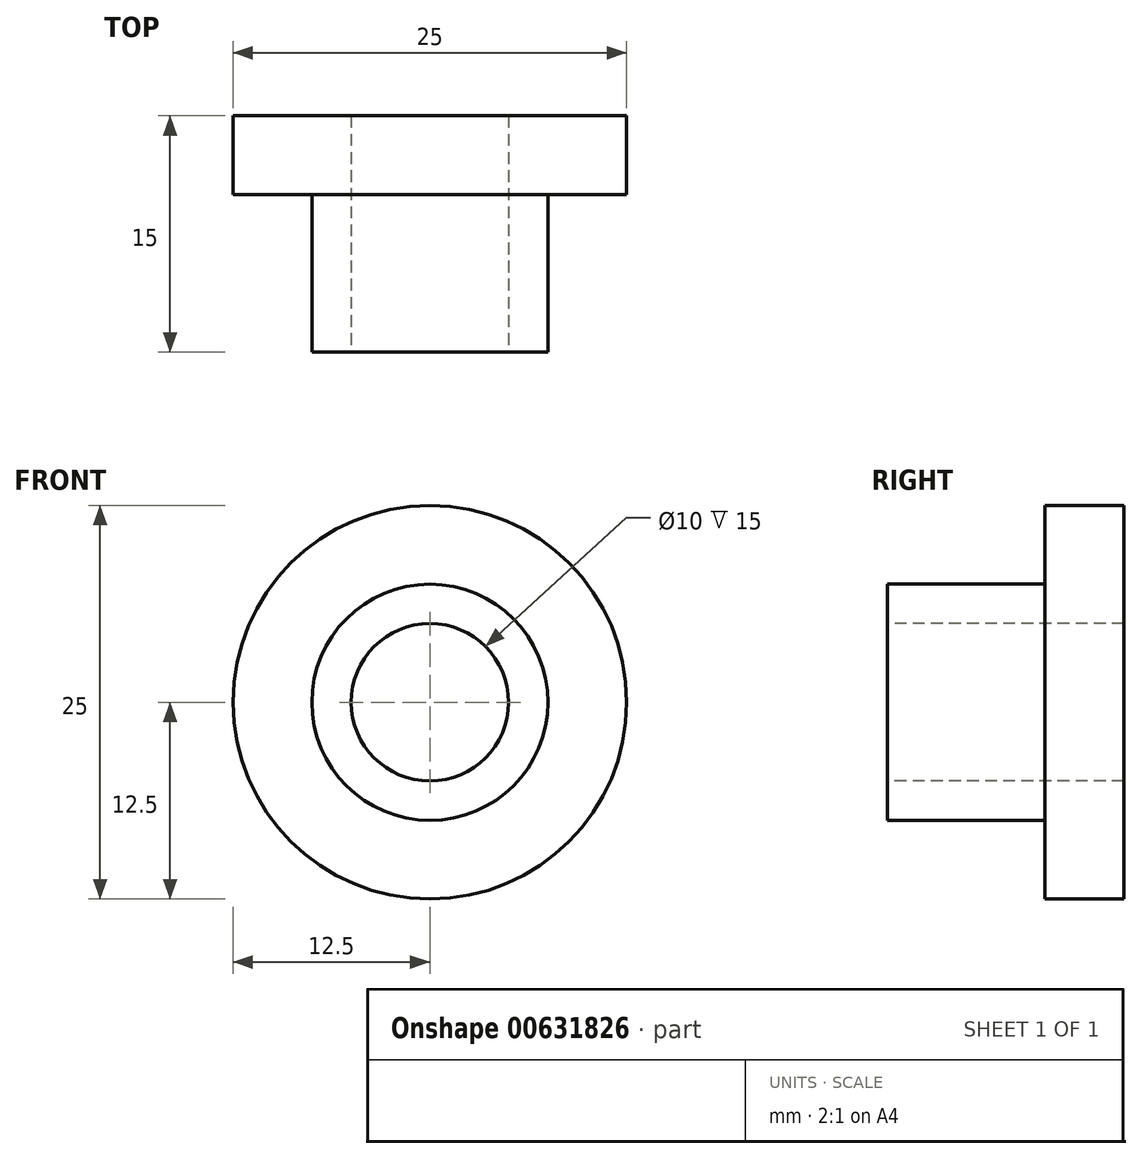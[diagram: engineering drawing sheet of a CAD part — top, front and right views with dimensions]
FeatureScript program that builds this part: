
annotation { "Feature Type Name" : "Feature", "Feature Type Description" : "" }
export const myFeature = defineFeature(function(context is Context, id is Id, definition is map)
    precondition{}
    {
        {
            var Q0;
            Q0=qCreatedBy(makeId("Front.planeOp"),FACE);
            var sketch = newSketch(context, id + "F0", { "sketchPlane" : qUnion([Q0])});
            skCircle(sketch, "E0", {"center": v(0, 0) * mm, "radius": 12.5 * mm});
            skSolve(sketch);
        }
        {
            var Q0;
            Q0 = qSketchRegion(id + "F0", true);
            extrude(context, id + "F1", {"entities" : qUnion([Q0]), "depth" : 5 * mm, "offsetDistance" : 25 * mm});
        }
        {
            var Q0;
            Q0=makeQuery(id+"F1.opExtrude","CAP_FACE",FACE,{"disambiguationData":[OSD([sQuery(id+"F0.wireOp",EDGE,"E0")])],"isStart":false});
            var sketch = newSketch(context, id + "F2", { "sketchPlane" : qUnion([Q0])});
            skCircle(sketch, "E1", {"center": v(0, 0) * mm, "radius": 7.5 * mm});
            skSolve(sketch);
        }
        {
            var Q0;
            Q0=makeQuery(id+"F2.imprint","IMPRINT",FACE,{"disambiguationData":[TD([[makeQuery(id+"F2.imprint","IMPRINT",EDGE,{"derivedFrom":sQuery(id+"F2.wireOp",EDGE,"E1")}),1.0]])]});
            extrude(context, id + "F3", {"entities" : qUnion([Q0]), "operationType" : NewBodyOperationType.ADD, "depth" : 10 * mm, "offsetDistance" : 25 * mm});
        }
        {
            var Q0;
            Q0=makeQuery(id+"F3.opExtrude","CAP_FACE",FACE,{"disambiguationData":[OSD([sQuery(id+"F2.wireOp",EDGE,"E1")])],"isStart":false});
            var sketch = newSketch(context, id + "F4", { "sketchPlane" : qUnion([Q0])});
            skCircle(sketch, "E2", {"center": v(0, 0) * mm, "radius": 5 * mm});
            skSolve(sketch);
        }
        {
            var Q0;
            Q0 = qSketchRegion(id + "F4", true);
            extrude(context, id + "F5", {"entities" : qUnion([Q0]), "operationType" : NewBodyOperationType.REMOVE, "endBound" : BoundingType.THROUGH_ALL, "oppositeDirection" : true, "depth" : 25 * mm, "offsetDistance" : 25 * mm});
        }
    });
